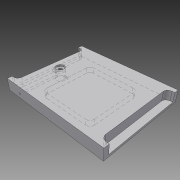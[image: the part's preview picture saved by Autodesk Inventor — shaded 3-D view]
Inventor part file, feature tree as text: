
AUTODESK INVENTOR PART (.ipt)
format: ipt  version: 2013 (Build 170138000, 138)  size: 148,992 bytes
history: native  units: mm
features: extrude x6, sketch x6, fillet x2, hole x2, plane x1
ambient origin geometry x8: Origin, YZ Plane, XZ Plane, XY Plane, X Axis, Y Axis, Z Axis, Center Point
bodies: Volumenkörper1 (feature_tree)
feature tree (17):
  extrude  "Extrusion1"  Depth=230.0mm
  plane  "Arbeitsebene1"
  extrude  "Extrusion2"  [1 undecoded]
  fillet  "Rundung1"  Radius=15.0mm
  extrude  "Extrusion3"  Depth=15.0mm
  fillet  "Rundung2"  Radius=160.0mm
  extrude  "Extrusion6"  Depth=116.0mm
  extrude  "Extrusion7"  Depth=12.0mm TaperAngle=0.0deg
  extrude  "Extrusion8"  Depth=20.0mm
  hole  "Bohrung4"  [1 undecoded]
  hole  "Bohrung5"  [1 undecoded]
  sketch  "Skizze1"  dims[d0=180.0mm d2=230.0mm]
  sketch  "Skizze2"  dims[d3=25.0mm d4=0.0mm d5=-90.0mm d6=15.0mm]
  sketch  "Skizze4"  dims[d8=20.0mm d9=15.0mm d10=160.0mm d11=0.0mm]
  sketch  "Skizze7"  dims[d12=10.0mm d16=116.0mm]
  sketch  "Skizze8"  dims[d18=116.0mm d19=12.0mm d20=0.0mm]
  sketch  "Skizze9"  dims[d21=10.0mm d62=20.0mm d65=4.0mm d66=0.0mm d67=18.0mm d68=0.0mm d69=8.0mm d71=5.0mm d72=0.0mm d74=21.0mm d75=15.0mm d76=70.0mm d77=4.0mm d78=6.0mm d79=6.0mm d80=7.0mm d81=90.0deg d82=50.0mm d83=20.594885mm d84=10.0mm d85=36.0mm d86=4.0mm d87=6.0mm d88=4.0mm d89=2.0mm d90=90.0deg d91=90.0mm d92=20.594885mm]
note: 3 required parameter values undecoded (feature->parameter linkage not recoverable at this tier; creation-order binding heuristic only, values carry confidence <= 0.55)
